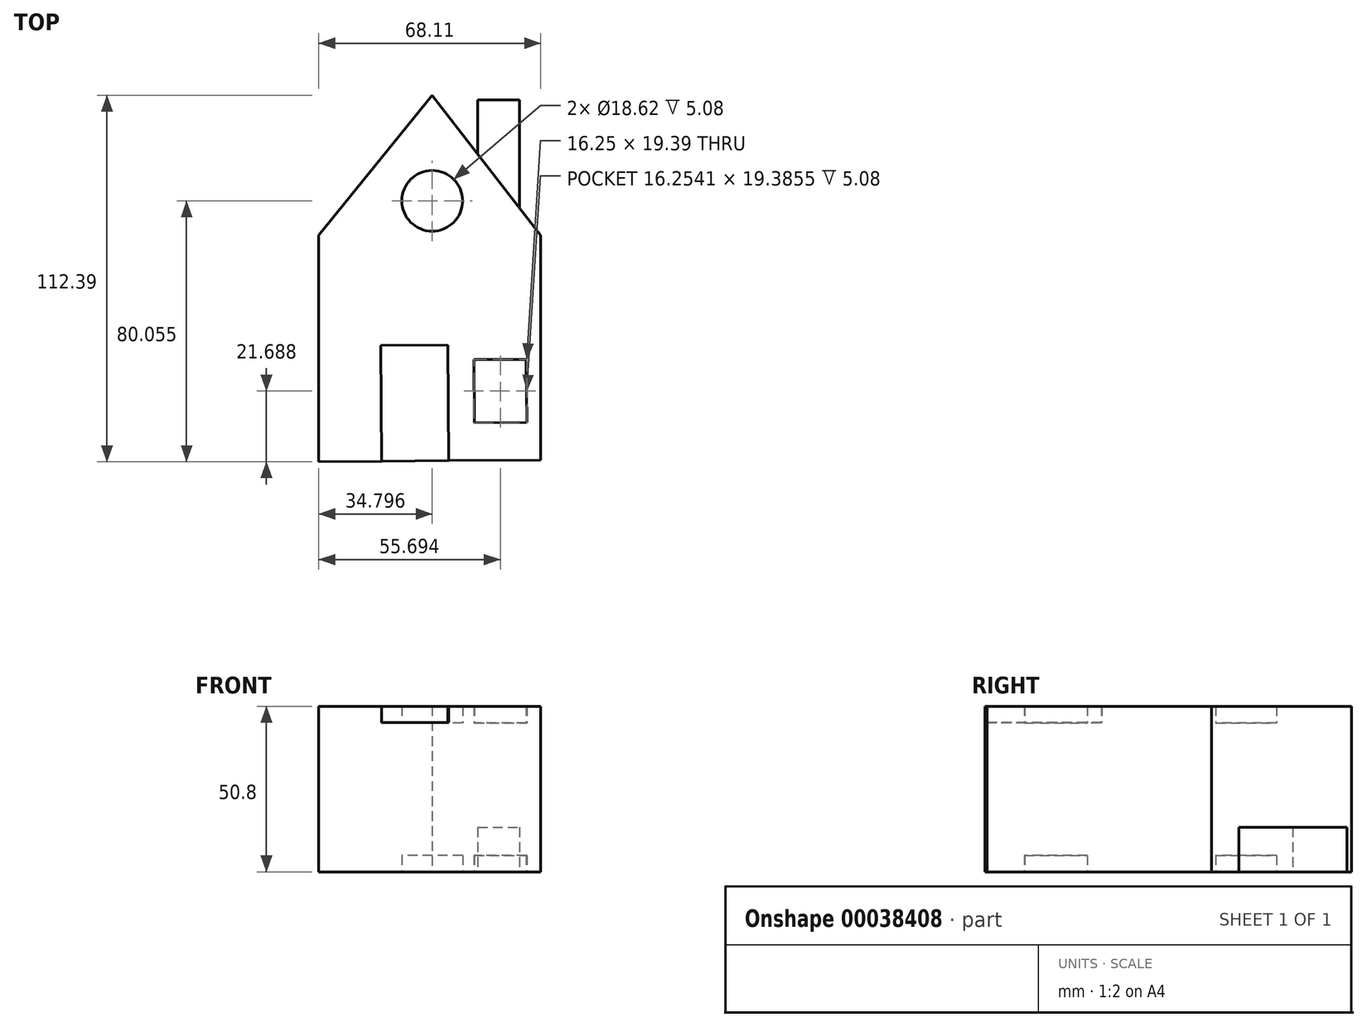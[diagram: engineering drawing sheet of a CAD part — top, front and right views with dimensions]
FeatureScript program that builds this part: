
annotation { "Feature Type Name" : "Feature", "Feature Type Description" : "" }
export const myFeature = defineFeature(function(context is Context, id is Id, definition is map)
    precondition{}
    {
        {
            var Q0;
            Q0=qCreatedBy(makeId("Top.planeOp"),FACE);
            var sketch = newSketch(context, id + "F0", { "sketchPlane" : qUnion([Q0])});
            skLineSegment(sketch, "E0", {"start": v(-51.34, -69.46) * mm, "end": v(-51.34, 0) * mm});
            skLineSegment(sketch, "E1", {"start": v(-51.34, 0) * mm, "end": v(-16.54, 42.93) * mm});
            skLineSegment(sketch, "E2", {"start": v(-16.54, 42.93) * mm, "end": v(16.77, 0) * mm});
            skLineSegment(sketch, "E3", {"start": v(16.77, 0) * mm, "end": v(16.77, -68.89) * mm});
            skLineSegment(sketch, "E4", {"start": v(-2.55, 24.89) * mm, "end": v(-2.55, 41.5) * mm});
            skLineSegment(sketch, "E5", {"start": v(-2.55, 41.5) * mm, "end": v(10.27, 41.5) * mm});
            skLineSegment(sketch, "E6", {"start": v(10.27, 41.5) * mm, "end": v(10.27, 8.37) * mm});
            skLineSegment(sketch, "E7", {"start": v(10.27, 8.37) * mm, "end": v(-2.55, 24.89) * mm});
            skLineSegment(sketch, "E8", {"start": v(-32.02, -69.3) * mm, "end": v(-32.32, -33.8) * mm});
            skLineSegment(sketch, "E9", {"start": v(-32.32, -33.8) * mm, "end": v(-11.77, -33.64) * mm});
            skLineSegment(sketch, "E10", {"start": v(-11.77, -33.64) * mm, "end": v(-11.48, -69.12) * mm});
            skLineSegment(sketch, "E11", {"start": v(-3.77, -38.08) * mm, "end": v(-3.61, -57.47) * mm});
            skLineSegment(sketch, "E12", {"start": v(-3.61, -57.47) * mm, "end": v(12.48, -57.33) * mm});
            skLineSegment(sketch, "E13", {"start": v(12.48, -57.33) * mm, "end": v(12.32, -38.09) * mm});
            skLineSegment(sketch, "E14", {"start": v(12.32, -38.09) * mm, "end": v(-3.77, -38.08) * mm});
            skLineSegment(sketch, "E15", {"start": v(16.77, -68.89) * mm, "end": v(-11.48, -69.12) * mm});
            skLineSegment(sketch, "E16", {"start": v(-32.02, -69.3) * mm, "end": v(-51.34, -69.46) * mm});
            skLineSegment(sketch, "E17", {"start": v(-32.02, -69.3) * mm, "end": v(-11.48, -69.12) * mm});
            skCircle(sketch, "E18", {"center": v(-16.54, 10.6) * mm, "radius": 9.3 * mm});
            skSolve(sketch);
        }
        {
            var Q0;
            {var subQ17=sQuery(id+"F0.wireOp",EDGE,"E0");Q0=makeQuery(id+"F0.imprint","IMPRINT",FACE,{"disambiguationData":[TD([[makeQuery(id+"F0.imprint","IMPRINT",EDGE,{"derivedFrom":subQ17}),-1.0]])]});}
            extrude(context, id + "F1", {"entities" : qUnion([Q0]), "depth" : 50.8 * mm});
        }
        {
            var Q0;
            Q0=makeQuery(id+"F0.imprint","IMPRINT",FACE,{"disambiguationData":[TD([[makeQuery(id+"F0.imprint","IMPRINT",EDGE,{"derivedFrom":sQuery(id+"F0.wireOp",EDGE,"E4")}),-1.0]])]});
            extrude(context, id + "F2", {"entities" : qUnion([Q0]), "operationType" : NewBodyOperationType.ADD, "depth" : 13.67 * mm});
        }
        {
            var Q0;
            Q0=makeQuery(id+"F0.imprint","IMPRINT",FACE,{"disambiguationData":[TD([[makeQuery(id+"F0.imprint","IMPRINT",EDGE,{"derivedFrom":sQuery(id+"F0.wireOp",EDGE,"E8")}),-1.0]])]});
            extrude(context, id + "F3", {"entities" : qUnion([Q0]), "operationType" : NewBodyOperationType.ADD, "depth" : 45.84 * mm});
        }
        {
            var Q0;
            Q0=makeQuery(id+"F0.imprint","IMPRINT",FACE,{"disambiguationData":[TD([[makeQuery(id+"F0.imprint","IMPRINT",EDGE,{"derivedFrom":sQuery(id+"F0.wireOp",EDGE,"E11")}),1.0]])]});
            extrude(context, id + "F4", {"entities" : qUnion([Q0]), "operationType" : NewBodyOperationType.ADD, "depth" : 45.72 * mm, "hasSecondDirection" : true, "secondDirectionOppositeDirection" : false, "secondDirectionDepth" : 5.08 * mm});
        }
        {
            var Q0;
            Q0=makeQuery(id+"F0.imprint","IMPRINT",FACE,{"disambiguationData":[TD([[makeQuery(id+"F0.imprint","IMPRINT",EDGE,{"derivedFrom":sQuery(id+"F0.wireOp",EDGE,"E18")}),1.0]])]});
            extrude(context, id + "F5", {"entities" : qUnion([Q0]), "operationType" : NewBodyOperationType.ADD, "depth" : 45.72 * mm, "hasSecondDirection" : true, "secondDirectionOppositeDirection" : false, "secondDirectionDepth" : 5.08 * mm});
        }
    });
